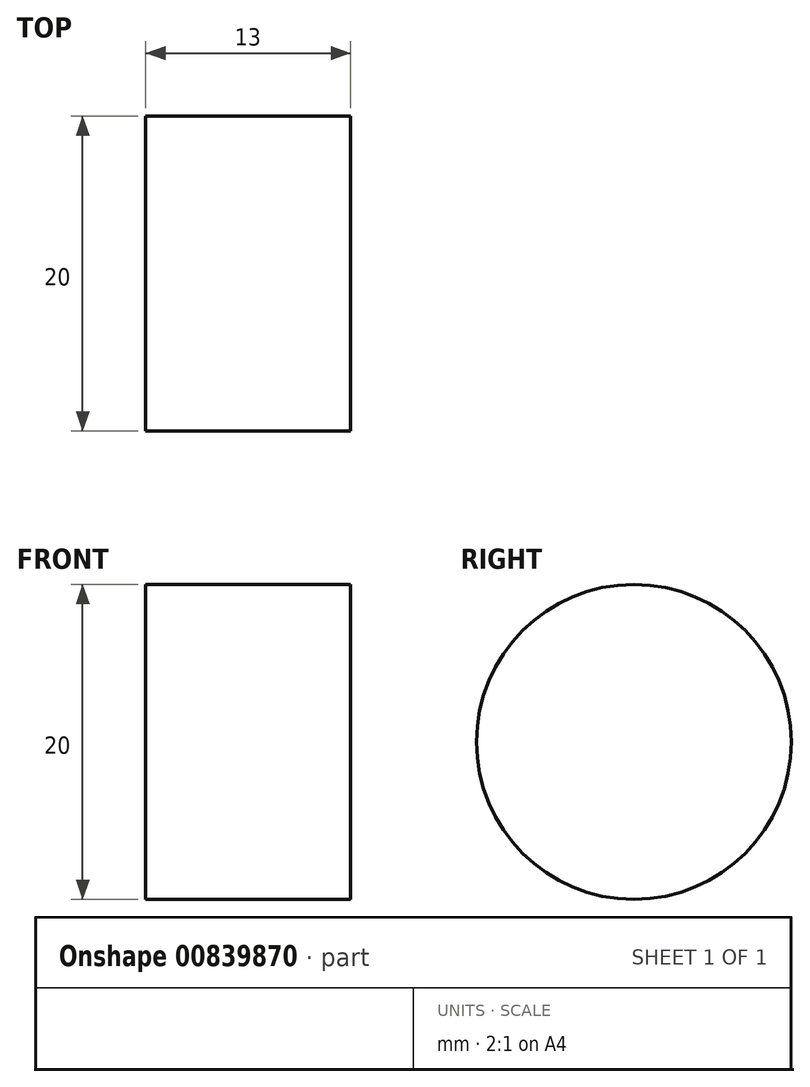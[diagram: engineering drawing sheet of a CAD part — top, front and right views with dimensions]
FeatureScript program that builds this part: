
annotation { "Feature Type Name" : "Feature", "Feature Type Description" : "" }
export const myFeature = defineFeature(function(context is Context, id is Id, definition is map)
    precondition{}
    {
        {
            var Q0;
            Q0=qCreatedBy(makeId("Right.planeOp"),FACE);
            var sketch = newSketch(context, id + "F0", { "sketchPlane" : qUnion([Q0])});
            skCircle(sketch, "E0", {"center": v(0, 0) * mm, "radius": 10 * mm});
            skSolve(sketch);
        }
        {
            var Q0;
            Q0=sQuery(id+"F0.wireOp",EDGE,"E0");
            extrude(context, id + "F1", {"bodyType" : ToolBodyType.SURFACE, "surfaceEntities" : qUnion([Q0]), "depth" : 13 * mm, "offsetDistance" : 25 * mm});
        }
    });
